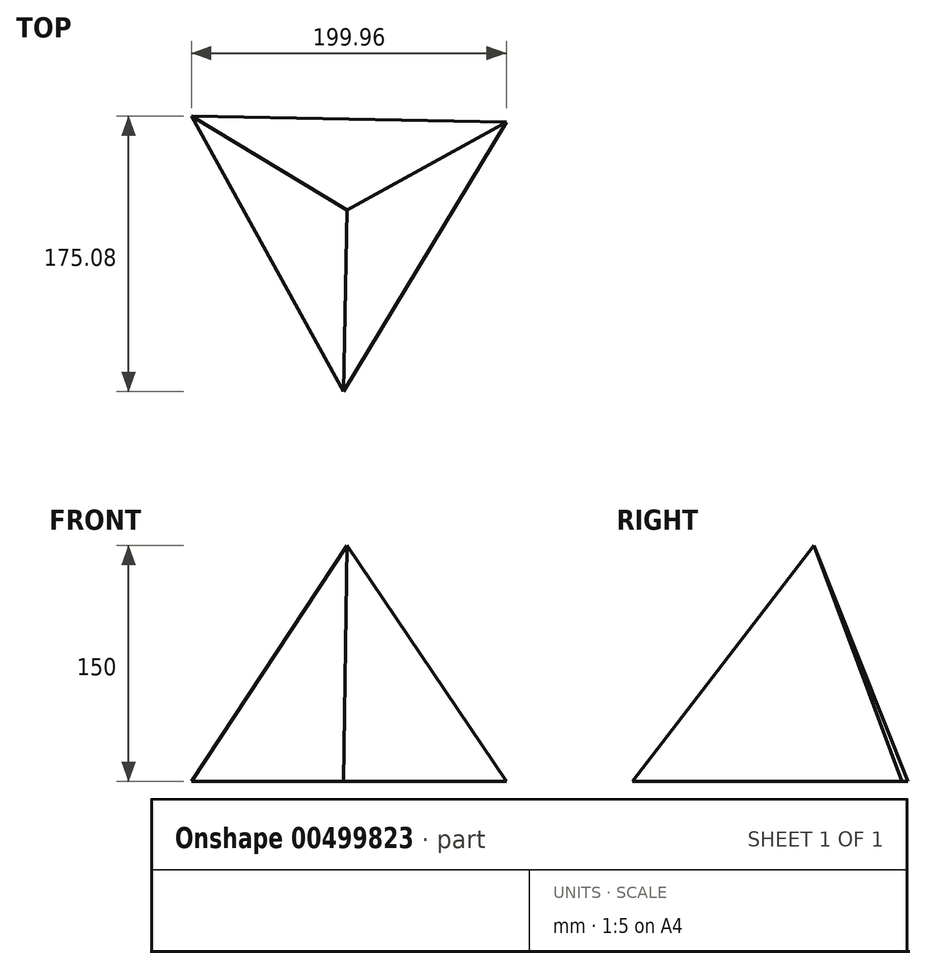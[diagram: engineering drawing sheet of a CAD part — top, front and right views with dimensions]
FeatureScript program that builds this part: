
annotation { "Feature Type Name" : "Feature", "Feature Type Description" : "" }
export const myFeature = defineFeature(function(context is Context, id is Id, definition is map)
    precondition{}
    {
        {
            var Q0;
            Q0=qCreatedBy(makeId("Top.planeOp"),FACE);
            var sketch = newSketch(context, id + "F0", { "sketchPlane" : qUnion([Q0])});
            skCircle(sketch, "E0.cCircle", {"center": v(0, 0) * mm, "radius": 115.47 * mm, "construction": true});
            skLineSegment(sketch, "E0.0", {"start": v(101.08, 55.82) * mm, "end": v(-2.2, -115.45) * mm});
            skLineSegment(sketch, "E0.1", {"start": v(-2.2, -115.45) * mm, "end": v(-98.88, 59.63) * mm});
            skLineSegment(sketch, "E0.2", {"start": v(-98.88, 59.63) * mm, "end": v(101.08, 55.82) * mm});
            skSolve(sketch);
        }
        {
            var Q0;
            Q0=qCreatedBy(makeId("Top.planeOp"),FACE);
            cPlane(context, id + "F1", {"entities" : qUnion([Q0]), "cplaneType" : CPlaneType.OFFSET, "offset" : 150 * mm, "width" : 150 * mm, "height" : 150 * mm});
        }
        {
            var Q0;
            Q0=qCreatedBy(id+"F1.planeOp",FACE);
            var sketch = newSketch(context, id + "F2", { "sketchPlane" : qUnion([Q0])});
            skPoint(sketch, "E1", {"position": v(0, 0) * mm});
            skSolve(sketch);
        }
        {
            var Q0;
            Q0=sQuery(id+"F2.wireOp",VERTEX,"E1");
            var Q1;
            Q1=makeQuery(id+"F0.imprint","IMPRINT",FACE,{"disambiguationData":[TD([[makeQuery(id+"F0.imprint","IMPRINT",EDGE,{"derivedFrom":sQuery(id+"F0.wireOp",EDGE,"E0.0")}),-1.0]])]});
            loft(context, id + "F3", {"sheetProfilesArray" : [{ "sheetProfileEntities" : qUnion([Q0]) }, { "sheetProfileEntities" : qUnion([Q1]) }]});
        }
    });
